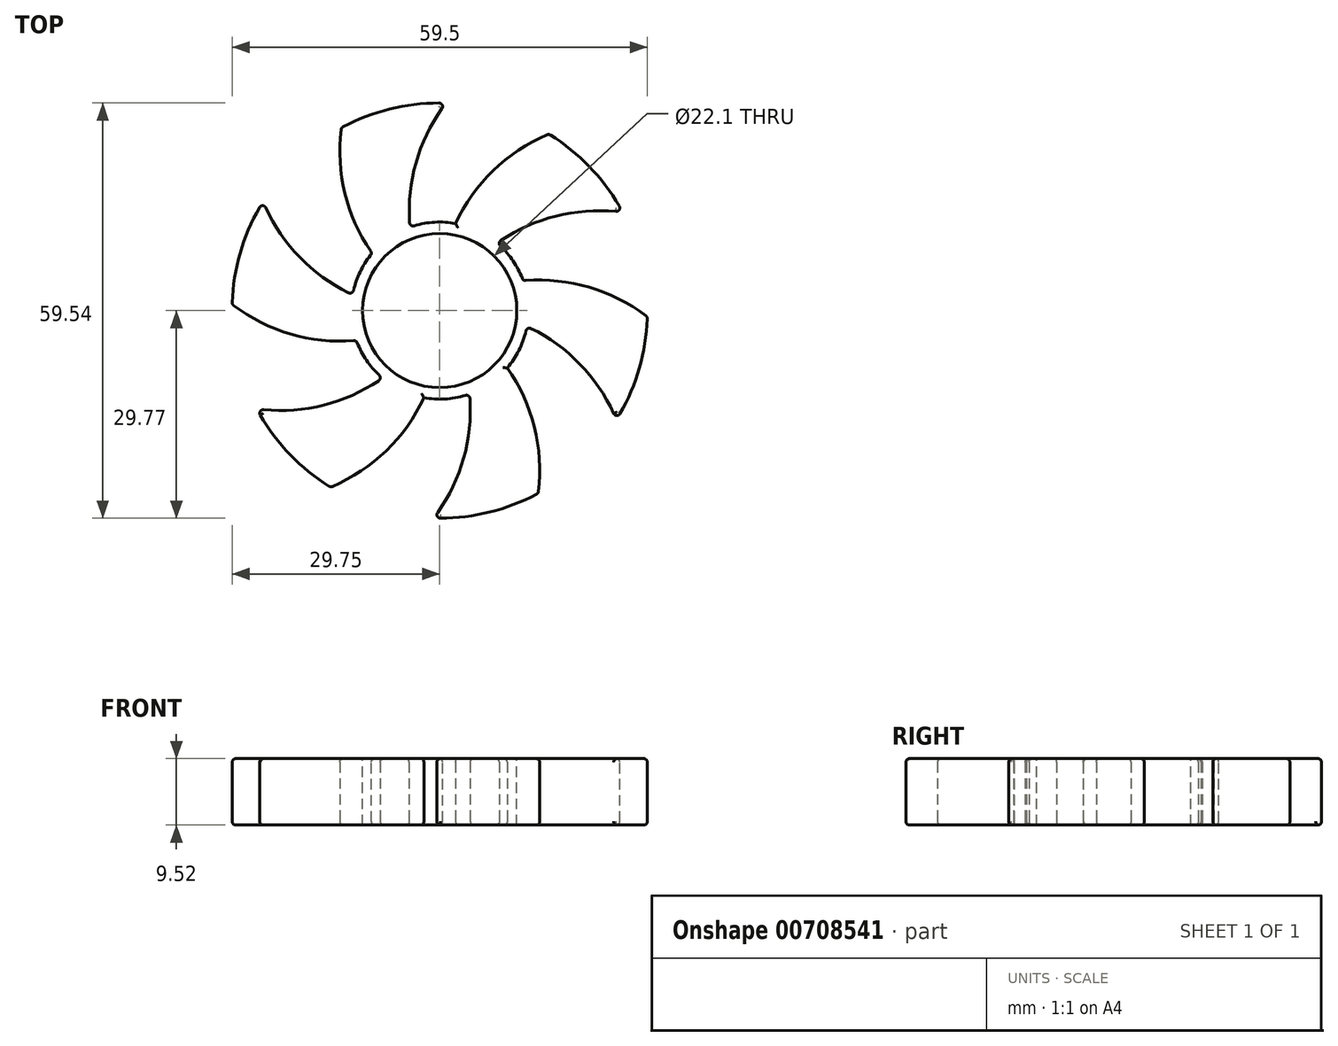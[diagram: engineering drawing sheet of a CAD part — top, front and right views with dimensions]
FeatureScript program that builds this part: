
annotation { "Feature Type Name" : "Feature", "Feature Type Description" : "" }
export const myFeature = defineFeature(function(context is Context, id is Id, definition is map)
    precondition{}
    {
        {
            var Q0;
            Q0=qCreatedBy(makeId("Top.planeOp"),FACE);
            var sketch = newSketch(context, id + "F0", { "sketchPlane" : qUnion([Q0])});
            skArc(sketch, "E0", {"start": v(-14.1, 26.22) * mm, "mid": v(-13.6, 16.8) * mm, "end": v(-9.68, 8.22) * mm});
            skArc(sketch, "E1.1.0", {"start": v(-25.33, 15.66) * mm, "mid": v(-20.17, 7.75) * mm, "end": v(-12.5, 2.28) * mm});
            skArc(sketch, "E1.2.0", {"start": v(-29.76, 0.9) * mm, "mid": v(-21.35, -3.37) * mm, "end": v(-11.96, -4.28) * mm});
            skArc(sketch, "E1.3.0", {"start": v(-26.22, -14.1) * mm, "mid": v(-16.8, -13.6) * mm, "end": v(-8.22, -9.68) * mm});
            skArc(sketch, "E1.4.0", {"start": v(-15.66, -25.33) * mm, "mid": v(-7.75, -20.17) * mm, "end": v(-2.28, -12.5) * mm});
            skArc(sketch, "E1.5.0", {"start": v(-0.9, -29.76) * mm, "mid": v(3.37, -21.35) * mm, "end": v(4.28, -11.96) * mm});
            skArc(sketch, "E1.6.0", {"start": v(14.1, -26.22) * mm, "mid": v(13.6, -16.8) * mm, "end": v(9.68, -8.22) * mm});
            skArc(sketch, "E1.7.0", {"start": v(25.33, -15.66) * mm, "mid": v(20.17, -7.75) * mm, "end": v(12.5, -2.28) * mm});
            skArc(sketch, "E1.8.0", {"start": v(29.76, -0.9) * mm, "mid": v(21.35, 3.37) * mm, "end": v(11.96, 4.28) * mm});
            skArc(sketch, "E1.9.0", {"start": v(26.22, 14.1) * mm, "mid": v(16.8, 13.6) * mm, "end": v(8.22, 9.68) * mm});
            skArc(sketch, "E1.10.0", {"start": v(15.66, 25.33) * mm, "mid": v(7.75, 20.17) * mm, "end": v(2.28, 12.5) * mm});
            skArc(sketch, "E1.11.0", {"start": v(0.9, 29.76) * mm, "mid": v(-3.37, 21.35) * mm, "end": v(-4.28, 11.96) * mm});
            skPoint(sketch, "E1.center", {"position": v(0, 0) * mm});
            skArc(sketch, "E2", {"start": v(0.9, 29.76) * mm, "mid": v(-6.84, 28.98) * mm, "end": v(-14.1, 26.22) * mm});
            skArc(sketch, "E3.trimOffspring", {"start": v(26.22, 14.1) * mm, "mid": v(21.68, 20.4) * mm, "end": v(15.66, 25.33) * mm});
            skArc(sketch, "E4.trimOffspring", {"start": v(25.33, -15.66) * mm, "mid": v(28.51, -8.57) * mm, "end": v(29.76, -0.9) * mm});
            skArc(sketch, "E5.trimOffspring", {"start": v(-0.9, -29.76) * mm, "mid": v(6.84, -28.98) * mm, "end": v(14.1, -26.22) * mm});
            skArc(sketch, "E6.trimOffspring", {"start": v(-26.22, -14.1) * mm, "mid": v(-21.68, -20.4) * mm, "end": v(-15.66, -25.33) * mm});
            skArc(sketch, "E7.trimOffspring", {"start": v(-25.33, 15.66) * mm, "mid": v(-28.51, 8.57) * mm, "end": v(-29.76, 0.9) * mm});
            skArc(sketch, "E8", {"start": v(-9.68, 8.22) * mm, "mid": v(-11.48, 5.43) * mm, "end": v(-12.5, 2.28) * mm});
            skArc(sketch, "E9.trimOffspring", {"start": v(2.28, 12.5) * mm, "mid": v(-1.04, 12.66) * mm, "end": v(-4.28, 11.96) * mm});
            skArc(sketch, "E10.trimOffspring", {"start": v(11.96, 4.28) * mm, "mid": v(10.44, 7.23) * mm, "end": v(8.22, 9.68) * mm});
            skArc(sketch, "E11.trimOffspring", {"start": v(9.68, -8.22) * mm, "mid": v(11.48, -5.43) * mm, "end": v(12.5, -2.28) * mm});
            skArc(sketch, "E12.trimOffspring", {"start": v(-2.28, -12.5) * mm, "mid": v(1.04, -12.66) * mm, "end": v(4.28, -11.96) * mm});
            skArc(sketch, "E13.trimOffspring", {"start": v(-11.96, -4.28) * mm, "mid": v(-10.44, -7.23) * mm, "end": v(-8.22, -9.68) * mm});
            skSolve(sketch);
        }
        {
            var Q0;
            Q0 = qSketchRegion(id + "F0", true);
            extrude(context, id + "F1", {"entities" : qUnion([Q0]), "endBound" : BoundingType.SYMMETRIC, "depth" : 9.52 * mm, "offsetDistance" : 25.4 * mm});
        }
        {
            var Q0;
            Q0=makeQuery(id+"F1.opExtrude","CAP_EDGE",EDGE,{"disambiguationData":[OSD([sQuery(id+"F0.wireOp",EDGE,"E6.trimOffspring")])],"isStart":false});
            var Q1;
            Q1=makeQuery(id+"F1.opExtrude","CAP_EDGE",EDGE,{"disambiguationData":[OSD([sQuery(id+"F0.wireOp",EDGE,"E6.trimOffspring")])],"isStart":true});
            var Q2;
            Q2=makeQuery(id+"F1.opExtrude","CAP_EDGE",EDGE,{"disambiguationData":[OSD([sQuery(id+"F0.wireOp",EDGE,"E1.4.0")])],"isStart":false});
            var Q3;
            Q3=makeQuery(id+"F1.opExtrude","CAP_EDGE",EDGE,{"disambiguationData":[OSD([sQuery(id+"F0.wireOp",EDGE,"E1.4.0")])],"isStart":true});
            var Q4;
            Q4=makeQuery(id+"F1.opExtrude","SWEPT_EDGE",EDGE,{"disambiguationData":[OSD([sQuery(id+"F0.wireOp",EDGE,"E1.4.0"),sQuery(id+"F0.wireOp",EDGE,"E6.trimOffspring")])]});
            var Q5;
            Q5=makeQuery(id+"F1.opExtrude","CAP_FACE",FACE,{"disambiguationData":[OSD([sQuery(id+"F0.wireOp",EDGE,"E0"),sQuery(id+"F0.wireOp",EDGE,"E1.1.0"),sQuery(id+"F0.wireOp",EDGE,"E1.2.0"),sQuery(id+"F0.wireOp",EDGE,"E1.3.0"),sQuery(id+"F0.wireOp",EDGE,"E1.4.0"),sQuery(id+"F0.wireOp",EDGE,"E1.5.0"),sQuery(id+"F0.wireOp",EDGE,"E1.6.0"),sQuery(id+"F0.wireOp",EDGE,"E1.7.0"),sQuery(id+"F0.wireOp",EDGE,"E1.8.0"),sQuery(id+"F0.wireOp",EDGE,"E1.9.0"),sQuery(id+"F0.wireOp",EDGE,"E1.10.0"),sQuery(id+"F0.wireOp",EDGE,"E1.11.0"),sQuery(id+"F0.wireOp",EDGE,"E2"),sQuery(id+"F0.wireOp",EDGE,"E3.trimOffspring"),sQuery(id+"F0.wireOp",EDGE,"E4.trimOffspring"),sQuery(id+"F0.wireOp",EDGE,"E5.trimOffspring"),sQuery(id+"F0.wireOp",EDGE,"E6.trimOffspring"),sQuery(id+"F0.wireOp",EDGE,"E7.trimOffspring"),sQuery(id+"F0.wireOp",EDGE,"E8"),sQuery(id+"F0.wireOp",EDGE,"E9.trimOffspring"),sQuery(id+"F0.wireOp",EDGE,"E10.trimOffspring"),sQuery(id+"F0.wireOp",EDGE,"E11.trimOffspring"),sQuery(id+"F0.wireOp",EDGE,"E12.trimOffspring"),sQuery(id+"F0.wireOp",EDGE,"E13.trimOffspring")])],"isStart":false});
            var Q6;
            Q6=makeQuery(id+"F1.opExtrude","SWEPT_FACE",FACE,{"disambiguationData":[OSD([sQuery(id+"F0.wireOp",EDGE,"E1.7.0")])]});
            var Q7;
            Q7=makeQuery(id+"F1.opExtrude","SWEPT_FACE",FACE,{"disambiguationData":[OSD([sQuery(id+"F0.wireOp",EDGE,"E5.trimOffspring")])]});
            var Q8;
            Q8=makeQuery(id+"F1.opExtrude","SWEPT_FACE",FACE,{"disambiguationData":[OSD([sQuery(id+"F0.wireOp",EDGE,"E1.5.0")])]});
            var Q9;
            Q9=makeQuery(id+"F1.opExtrude","SWEPT_FACE",FACE,{"disambiguationData":[OSD([sQuery(id+"F0.wireOp",EDGE,"E1.2.0")])]});
            var Q10;
            Q10=makeQuery(id+"F1.opExtrude","SWEPT_FACE",FACE,{"disambiguationData":[OSD([sQuery(id+"F0.wireOp",EDGE,"E1.3.0")])]});
            var Q11;
            Q11=makeQuery(id+"F1.opExtrude","SWEPT_FACE",FACE,{"disambiguationData":[OSD([sQuery(id+"F0.wireOp",EDGE,"E1.1.0")])]});
            var Q12;
            Q12=makeQuery(id+"F1.opExtrude","SWEPT_FACE",FACE,{"disambiguationData":[OSD([sQuery(id+"F0.wireOp",EDGE,"E0")])]});
            var Q13;
            Q13=makeQuery(id+"F1.opExtrude","SWEPT_FACE",FACE,{"disambiguationData":[OSD([sQuery(id+"F0.wireOp",EDGE,"E1.8.0")])]});
            var Q14;
            Q14=makeQuery(id+"F1.opExtrude","SWEPT_FACE",FACE,{"disambiguationData":[OSD([sQuery(id+"F0.wireOp",EDGE,"E1.11.0")])]});
            var Q15;
            Q15=makeQuery(id+"F1.opExtrude","SWEPT_FACE",FACE,{"disambiguationData":[OSD([sQuery(id+"F0.wireOp",EDGE,"E1.9.0")])]});
            var Q16;
            Q16=makeQuery(id+"F1.opExtrude","SWEPT_EDGE",EDGE,{"disambiguationData":[OSD([sQuery(id+"F0.wireOp",EDGE,"E1.10.0"),sQuery(id+"F0.wireOp",EDGE,"E3.trimOffspring")])]});
            var Q17;
            Q17=makeQuery(id+"F1.opExtrude","CAP_FACE",FACE,{"disambiguationData":[OSD([sQuery(id+"F0.wireOp",EDGE,"E0"),sQuery(id+"F0.wireOp",EDGE,"E1.1.0"),sQuery(id+"F0.wireOp",EDGE,"E1.2.0"),sQuery(id+"F0.wireOp",EDGE,"E1.3.0"),sQuery(id+"F0.wireOp",EDGE,"E1.4.0"),sQuery(id+"F0.wireOp",EDGE,"E1.5.0"),sQuery(id+"F0.wireOp",EDGE,"E1.6.0"),sQuery(id+"F0.wireOp",EDGE,"E1.7.0"),sQuery(id+"F0.wireOp",EDGE,"E1.8.0"),sQuery(id+"F0.wireOp",EDGE,"E1.9.0"),sQuery(id+"F0.wireOp",EDGE,"E1.10.0"),sQuery(id+"F0.wireOp",EDGE,"E1.11.0"),sQuery(id+"F0.wireOp",EDGE,"E2"),sQuery(id+"F0.wireOp",EDGE,"E3.trimOffspring"),sQuery(id+"F0.wireOp",EDGE,"E4.trimOffspring"),sQuery(id+"F0.wireOp",EDGE,"E5.trimOffspring"),sQuery(id+"F0.wireOp",EDGE,"E6.trimOffspring"),sQuery(id+"F0.wireOp",EDGE,"E7.trimOffspring"),sQuery(id+"F0.wireOp",EDGE,"E8"),sQuery(id+"F0.wireOp",EDGE,"E9.trimOffspring"),sQuery(id+"F0.wireOp",EDGE,"E10.trimOffspring"),sQuery(id+"F0.wireOp",EDGE,"E11.trimOffspring"),sQuery(id+"F0.wireOp",EDGE,"E12.trimOffspring"),sQuery(id+"F0.wireOp",EDGE,"E13.trimOffspring")])],"isStart":true});
            fillet(context, id + "F2", {"entities" : qUnion([Q0, Q1, Q2, Q3, Q4, Q5, Q6, Q7, Q8, Q9, Q10, Q11, Q12, Q13, Q14, Q15, Q16, Q17]), "radius" : 0.5 * mm, "tangentPropagation" : true, "allowEdgeOverflow" : false});
        }
        {
            var Q0;
            Q0=makeQuery(id+"F1.opExtrude","CAP_FACE",FACE,{"disambiguationData":[OSD([sQuery(id+"F0.wireOp",EDGE,"E0"),sQuery(id+"F0.wireOp",EDGE,"E1.1.0"),sQuery(id+"F0.wireOp",EDGE,"E1.2.0"),sQuery(id+"F0.wireOp",EDGE,"E1.3.0"),sQuery(id+"F0.wireOp",EDGE,"E1.4.0"),sQuery(id+"F0.wireOp",EDGE,"E1.5.0"),sQuery(id+"F0.wireOp",EDGE,"E1.6.0"),sQuery(id+"F0.wireOp",EDGE,"E1.7.0"),sQuery(id+"F0.wireOp",EDGE,"E1.8.0"),sQuery(id+"F0.wireOp",EDGE,"E1.9.0"),sQuery(id+"F0.wireOp",EDGE,"E1.10.0"),sQuery(id+"F0.wireOp",EDGE,"E1.11.0"),sQuery(id+"F0.wireOp",EDGE,"E2"),sQuery(id+"F0.wireOp",EDGE,"E3.trimOffspring"),sQuery(id+"F0.wireOp",EDGE,"E4.trimOffspring"),sQuery(id+"F0.wireOp",EDGE,"E5.trimOffspring"),sQuery(id+"F0.wireOp",EDGE,"E6.trimOffspring"),sQuery(id+"F0.wireOp",EDGE,"E7.trimOffspring"),sQuery(id+"F0.wireOp",EDGE,"E8"),sQuery(id+"F0.wireOp",EDGE,"E9.trimOffspring"),sQuery(id+"F0.wireOp",EDGE,"E10.trimOffspring"),sQuery(id+"F0.wireOp",EDGE,"E11.trimOffspring"),sQuery(id+"F0.wireOp",EDGE,"E12.trimOffspring"),sQuery(id+"F0.wireOp",EDGE,"E13.trimOffspring")])],"isStart":false});
            var sketch = newSketch(context, id + "F3", { "sketchPlane" : qUnion([Q0])});
            skCircle(sketch, "E14", {"center": v(0, 0) * mm, "radius": 11.05 * mm});
            skSolve(sketch);
        }
        {
            var Q0;
            Q0 = qSketchRegion(id + "F3", true);
            extrude(context, id + "F4", {"entities" : qUnion([Q0]), "operationType" : NewBodyOperationType.REMOVE, "oppositeDirection" : true, "depth" : 25.4 * mm, "offsetDistance" : 25.4 * mm});
        }
    });
